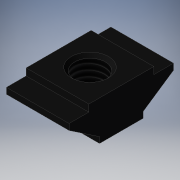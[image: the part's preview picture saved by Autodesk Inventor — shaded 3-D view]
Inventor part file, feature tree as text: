
AUTODESK INVENTOR PART (.ipt)
format: ipt  version: 2019 (Build 230136000, 136)  size: 134,656 bytes
history: native  units: mm
features: other x7, sketch x2, extrude x1, revolve x1, thread x1
ambient origin geometry x8: Origin, YZ Plane, XZ Plane, XY Plane, X Axis, Y Axis, Z Axis, Center Point
bodies: Solid1 (feature_tree)
feature tree (12):
  extrude  "Extrusion1"  TaperAngle=360.0deg  [1 undecoded]
  revolve  "Revolution1"  [1 undecoded]
  thread  "Thread1"  [1 undecoded]
  other  "TIN_4_XY"
  other  "TIN_4_YZ"
  other  "TIN_4_ZX"
  other  "TIN_4_X"
  other  "TIN_4_Y"
  other  "TIN_4_Z"
  other  "TIN_4_Center"
  sketch  "Skizze_1"  dims[d0=13.5mm d1=0.0mm d2=360.0deg]
  sketch  "Skizze_2"  dims[d3=7.147mm d4=0.0mm d5=0.0mm]
note: 3 required parameter values undecoded (feature->parameter linkage not recoverable at this tier; creation-order binding heuristic only, values carry confidence <= 0.55)